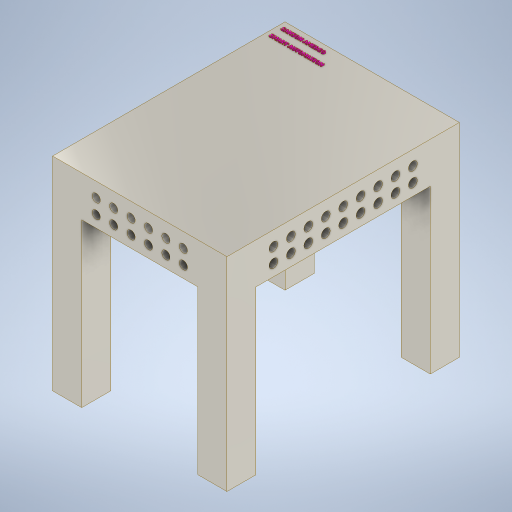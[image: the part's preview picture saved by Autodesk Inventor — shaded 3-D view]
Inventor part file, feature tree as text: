
AUTODESK INVENTOR PART (.ipt)
format: ipt  version: 2023 (Build 270158000, 158)  size: 865,280 bytes
history: native  units: mm
features: extrude x6, sketch x4, pattern_linear x2
ambient origin geometry x8: Origin, YZ Plane, XZ Plane, XY Plane, X Axis, Y Axis, Z Axis, Center Point
bodies: Body1 (feature_tree)
feature tree (12):
  sketch  "Schizzo1"
  extrude  "Estrusione5"  Depth=350.0mm TaperAngle=0.0deg
  extrude  "Estrusione6"  Depth=340.0mm TaperAngle=0.0deg
  extrude  "Estrusione7"  Depth=280.0mm TaperAngle=0.0deg
  extrude  "Estrusione9"  Depth=400.0mm
  pattern_linear  "Serie rettangolare1"  Count1=30  [1 undecoded]
  extrude  "Estrusione10"  Depth=50.0mm
  pattern_linear  "Serie rettangolare2"  Spacing1=15.0mm  [1 undecoded]
  extrude  "Estrusione11"  Depth=30.0mm
  sketch  "Schizzo6"
  sketch  "Schizzo7"
  sketch  "Schizzo9"
note: 2 required parameter values undecoded (feature->parameter linkage not recoverable at this tier; creation-order binding heuristic only, values carry confidence <= 0.55)
